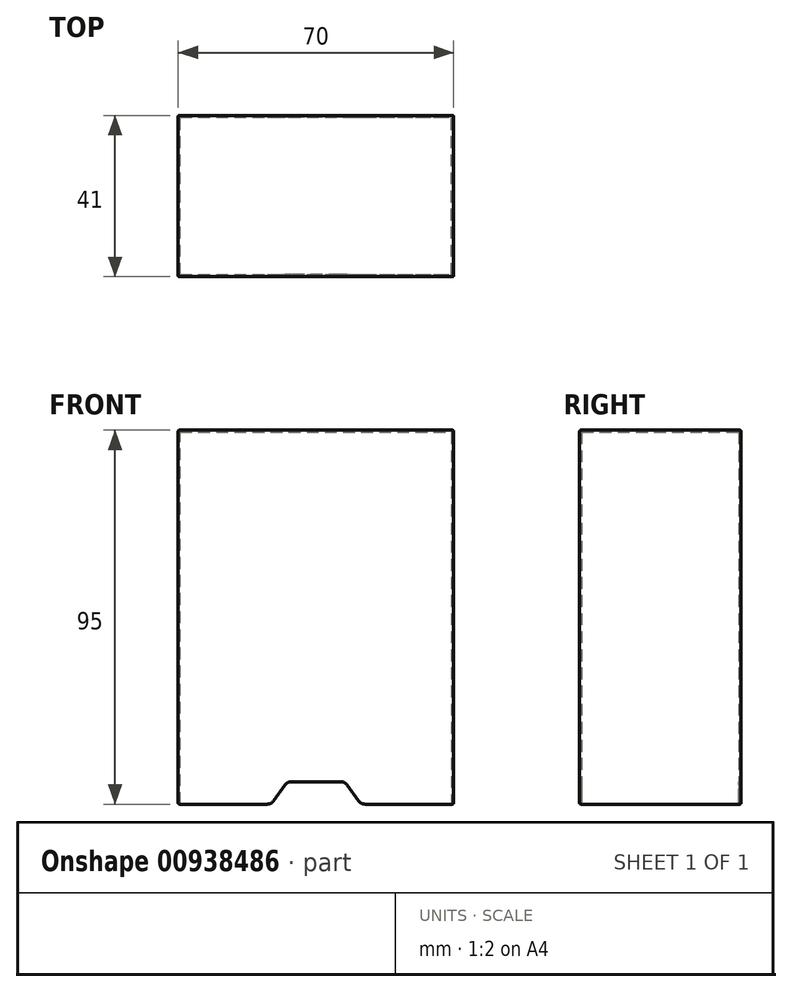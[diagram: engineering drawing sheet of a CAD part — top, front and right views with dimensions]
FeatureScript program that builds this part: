
annotation { "Feature Type Name" : "Feature", "Feature Type Description" : "" }
export const myFeature = defineFeature(function(context is Context, id is Id, definition is map)
    precondition{}
    {
        {
            var Q0;
            Q0=qCreatedBy(makeId("Front.planeOp"),FACE);
            var sketch = newSketch(context, id + "F0", { "sketchPlane" : qUnion([Q0])});
            skLineSegment(sketch, "E0", {"start": v(9.8, 0) * mm, "end": v(9.8, 95) * mm});
            skLineSegment(sketch, "E1", {"start": v(9.8, 95) * mm, "end": v(79.8, 95) * mm});
            skLineSegment(sketch, "E2", {"start": v(79.8, 95) * mm, "end": v(79.8, 0) * mm});
            skLineSegment(sketch, "E3", {"start": v(34.09, 0.83) * mm, "end": v(37, 4.88) * mm});
            skLineSegment(sketch, "E4", {"start": v(44.86, 5.71) * mm, "end": v(38.62, 5.71) * mm});
            skArc(sketch, "E5.filletArc", {"start": v(38.62, 5.71) * mm, "mid": v(37.7, 5.5) * mm, "end": v(37, 4.88) * mm});
            skLineSegment(sketch, "E6", {"start": v(9.8, 0) * mm, "end": v(32.46, 0) * mm});
            skArc(sketch, "E7.filletArc", {"start": v(32.46, 0) * mm, "mid": v(33.37, 0.22) * mm, "end": v(34.09, 0.83) * mm});
            skLineSegment(sketch, "E8", {"start": v(52.73, 4.88) * mm, "end": v(55.63, 0.83) * mm});
            skLineSegment(sketch, "E9", {"start": v(51.1, 5.71) * mm, "end": v(44.86, 5.71) * mm});
            skArc(sketch, "E10.filletArc", {"start": v(52.73, 4.88) * mm, "mid": v(52.01, 5.5) * mm, "end": v(51.1, 5.71) * mm});
            skLineSegment(sketch, "E11", {"start": v(57.26, 0) * mm, "end": v(79.8, 0) * mm});
            skArc(sketch, "E12.filletArc", {"start": v(55.63, 0.83) * mm, "mid": v(56.34, 0.22) * mm, "end": v(57.26, 0) * mm});
            skSolve(sketch);
        }
        {
            var Q0;
            Q0 = qSketchRegion(id + "F0", true);
            var Q1;
            Q1=makeQuery(id+"Fw6wdvTFKlkDJ6P_0.imprint","IMPRINT",FACE,{"disambiguationData":[TD([[makeQuery(id+"Fw6wdvTFKlkDJ6P_0.imprint","IMPRINT",EDGE,{"derivedFrom":sQuery(id+"Fw6wdvTFKlkDJ6P_0.wireOp",EDGE,"32353973-848b-4fb8-a84b-607301a58f47")}),1.0]])]});
            extrude(context, id + "F1", {"entities" : qUnion([Q0, Q1]), "depth" : 41 * mm, "offsetDistance" : 25 * mm});
        }
        {
            var Q0;
            Q0=makeQuery(id+"F1.opExtrude","SWEPT_FACE",FACE,{"disambiguationData":[OSD([sQuery(id+"F0.wireOp",EDGE,"E6")])]});
            var Q1;
            Q1=makeQuery(id+"F1.opExtrude","SWEPT_FACE",FACE,{"disambiguationData":[OSD([sQuery(id+"F0.wireOp",EDGE,"E7.filletArc")])]});
            var Q2;
            Q2=makeQuery(id+"F1.opExtrude","SWEPT_FACE",FACE,{"disambiguationData":[OSD([sQuery(id+"F0.wireOp",EDGE,"E3")])]});
            var Q3;
            Q3=makeQuery(id+"F1.opExtrude","SWEPT_FACE",FACE,{"disambiguationData":[OSD([sQuery(id+"F0.wireOp",EDGE,"E5.filletArc")])]});
            var Q4;
            Q4=makeQuery(id+"F1.opExtrude","SWEPT_FACE",FACE,{"disambiguationData":[OSD([sQuery(id+"F0.wireOp",EDGE,"E4"),sQuery(id+"F0.wireOp",EDGE,"E9")])]});
            var Q5;
            Q5=makeQuery(id+"F1.opExtrude","SWEPT_FACE",FACE,{"disambiguationData":[OSD([sQuery(id+"F0.wireOp",EDGE,"E10.filletArc")])]});
            var Q6;
            Q6=makeQuery(id+"F1.opExtrude","SWEPT_FACE",FACE,{"disambiguationData":[OSD([sQuery(id+"F0.wireOp",EDGE,"E12.filletArc")])]});
            var Q7;
            Q7=makeQuery(id+"F1.opExtrude","SWEPT_FACE",FACE,{"disambiguationData":[OSD([sQuery(id+"F0.wireOp",EDGE,"E11")])]});
            var Q8;
            Q8=makeQuery(id+"F1.opExtrude","SWEPT_FACE",FACE,{"disambiguationData":[OSD([sQuery(id+"F0.wireOp",EDGE,"E8")])]});
            shell(context, id + "F2", {"entities" : qUnion([Q0, Q1, Q2, Q3, Q4, Q5, Q6, Q7, Q8]), "thickness" : 0.5 * mm});
        }
        {
            var Q0;
            Q0=makeQuery(id+"F1.opExtrude","CAP_EDGE",EDGE,{"disambiguationData":[OSD([sQuery(id+"F0.wireOp",EDGE,"E1")])],"isStart":false});
            var Q1;
            Q1=makeQuery(id+"F1.opExtrude","CAP_EDGE",EDGE,{"disambiguationData":[OSD([sQuery(id+"F0.wireOp",EDGE,"E0")])],"isStart":false});
            fillet(context, id + "F3", {"entities" : qUnion([Q0, Q1]), "tangentPropagation" : true, "radius" : 0.3 * mm, "defaultsChanged" : false, "vertexSettings" : [], "allowEdgeOverflow" : false});
        }
        {
            var Q0;
            Q0=makeQuery(id+"F1.opExtrude","SWEPT_EDGE",EDGE,{"disambiguationData":[OSD([sQuery(id+"F0.wireOp",EDGE,"E0"),sQuery(id+"F0.wireOp",EDGE,"E1")])]});
            var Q1;
            Q1=makeQuery(id+"F1.opExtrude","CAP_EDGE",EDGE,{"disambiguationData":[OSD([sQuery(id+"F0.wireOp",EDGE,"E1")])],"isStart":true});
            var Q2;
            Q2=makeQuery(id+"F1.opExtrude","SWEPT_EDGE",EDGE,{"disambiguationData":[OSD([sQuery(id+"F0.wireOp",EDGE,"E1"),sQuery(id+"F0.wireOp",EDGE,"E2")])]});
            var Q3;
            Q3=makeQuery(id+"F1.opExtrude","CAP_EDGE",EDGE,{"disambiguationData":[OSD([sQuery(id+"F0.wireOp",EDGE,"E0")])],"isStart":true});
            var Q4;
            Q4=makeQuery(id+"F1.opExtrude","CAP_EDGE",EDGE,{"disambiguationData":[OSD([sQuery(id+"F0.wireOp",EDGE,"E2")])],"isStart":true});
            var Q5;
            Q5=makeQuery(id+"F1.opExtrude","CAP_EDGE",EDGE,{"disambiguationData":[OSD([sQuery(id+"F0.wireOp",EDGE,"E6")])],"isStart":false});
            var Q6;
            Q6=makeQuery(id+"F1.opExtrude","CAP_EDGE",EDGE,{"disambiguationData":[OSD([sQuery(id+"F0.wireOp",EDGE,"E7.filletArc")])],"isStart":false});
            var Q7;
            Q7=makeQuery(id+"F1.opExtrude","CAP_EDGE",EDGE,{"disambiguationData":[OSD([sQuery(id+"F0.wireOp",EDGE,"E3")])],"isStart":false});
            var Q8;
            Q8=makeQuery(id+"F1.opExtrude","CAP_EDGE",EDGE,{"disambiguationData":[OSD([sQuery(id+"F0.wireOp",EDGE,"E11")])],"isStart":false});
            var Q9;
            Q9=makeQuery(id+"F1.opExtrude","SWEPT_EDGE",EDGE,{"disambiguationData":[OSD([sQuery(id+"F0.wireOp",EDGE,"E2"),sQuery(id+"F0.wireOp",EDGE,"E11")])]});
            var Q10;
            Q10=makeQuery(id+"F1.opExtrude","CAP_EDGE",EDGE,{"disambiguationData":[OSD([sQuery(id+"F0.wireOp",EDGE,"E6")])],"isStart":true});
            fillet(context, id + "F4", {"entities" : qUnion([Q0, Q1, Q2, Q3, Q4, Q5, Q6, Q7, Q8, Q9, Q10]), "tangentPropagation" : true, "radius" : 0.3 * mm, "defaultsChanged" : false, "vertexSettings" : [], "allowEdgeOverflow" : false});
        }
    });
